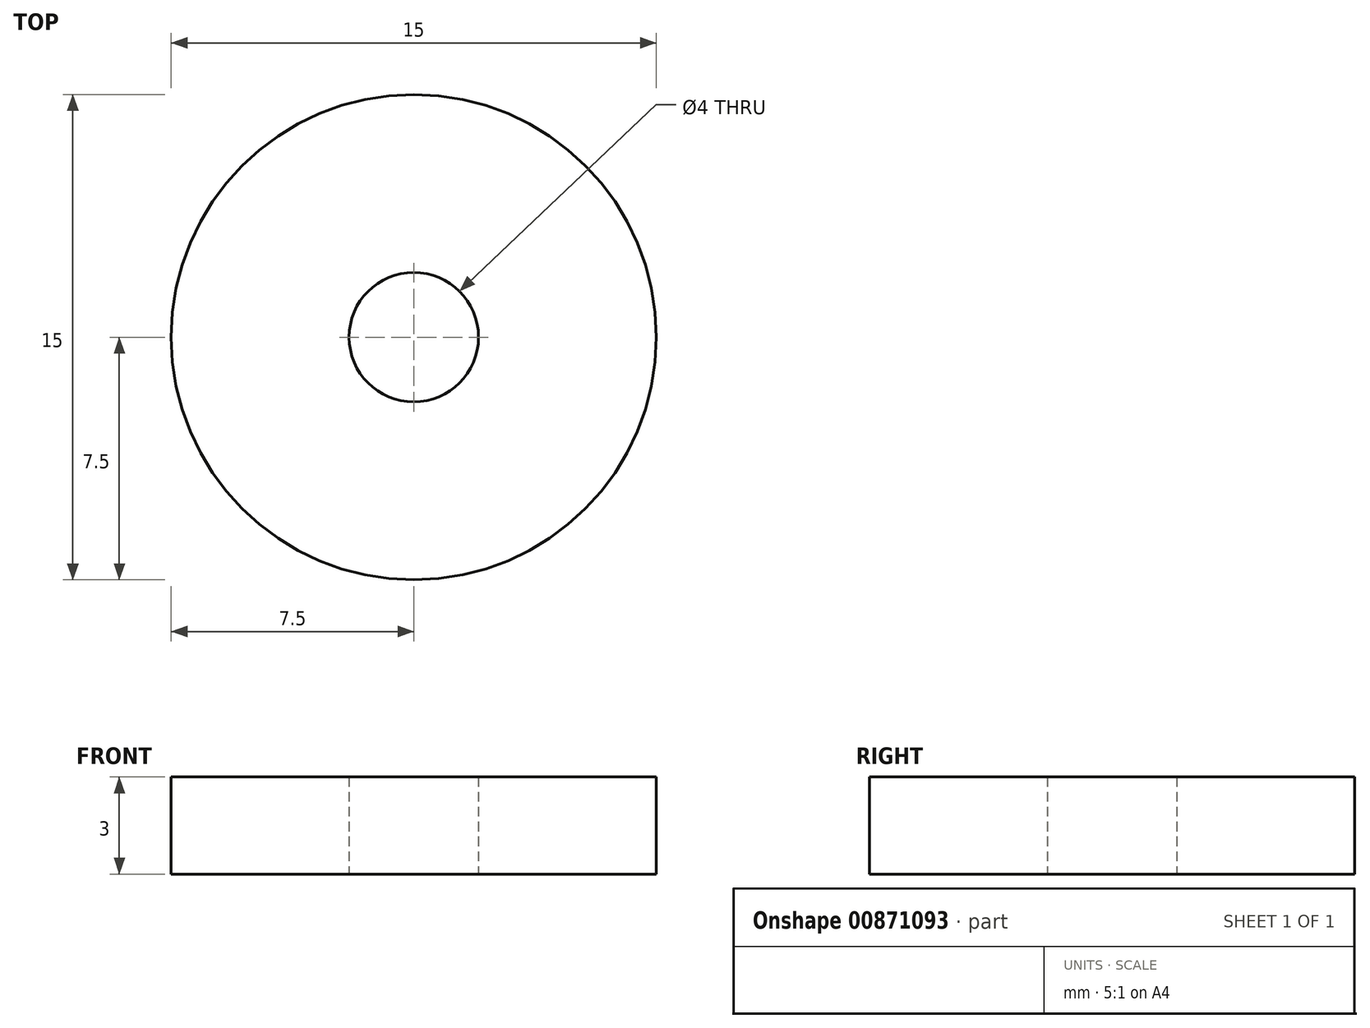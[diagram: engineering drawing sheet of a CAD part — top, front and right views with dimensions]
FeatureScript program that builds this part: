
annotation { "Feature Type Name" : "Feature", "Feature Type Description" : "" }
export const myFeature = defineFeature(function(context is Context, id is Id, definition is map)
    precondition{}
    {
        {
            var Q0;
            Q0=qCreatedBy(makeId("Top.planeOp"),FACE);
            var sketch = newSketch(context, id + "F0", { "sketchPlane" : qUnion([Q0])});
            skCircle(sketch, "E0", {"center": v(0, 0) * mm, "radius": 2 * mm});
            skCircle(sketch, "E1", {"center": v(0, 0) * mm, "radius": 7.5 * mm});
            skSolve(sketch);
        }
        {
            var Q0;
            Q0=makeQuery(id+"F0.imprint","IMPRINT",FACE,{"disambiguationData":[TD([[makeQuery(id+"F0.imprint","IMPRINT",EDGE,{"derivedFrom":sQuery(id+"F0.wireOp",EDGE,"E0")}),-1.0]])]});
            extrude(context, id + "F1", {"entities" : qUnion([Q0]), "depth" : 3 * mm, "offsetDistance" : 25 * mm});
        }
    });
